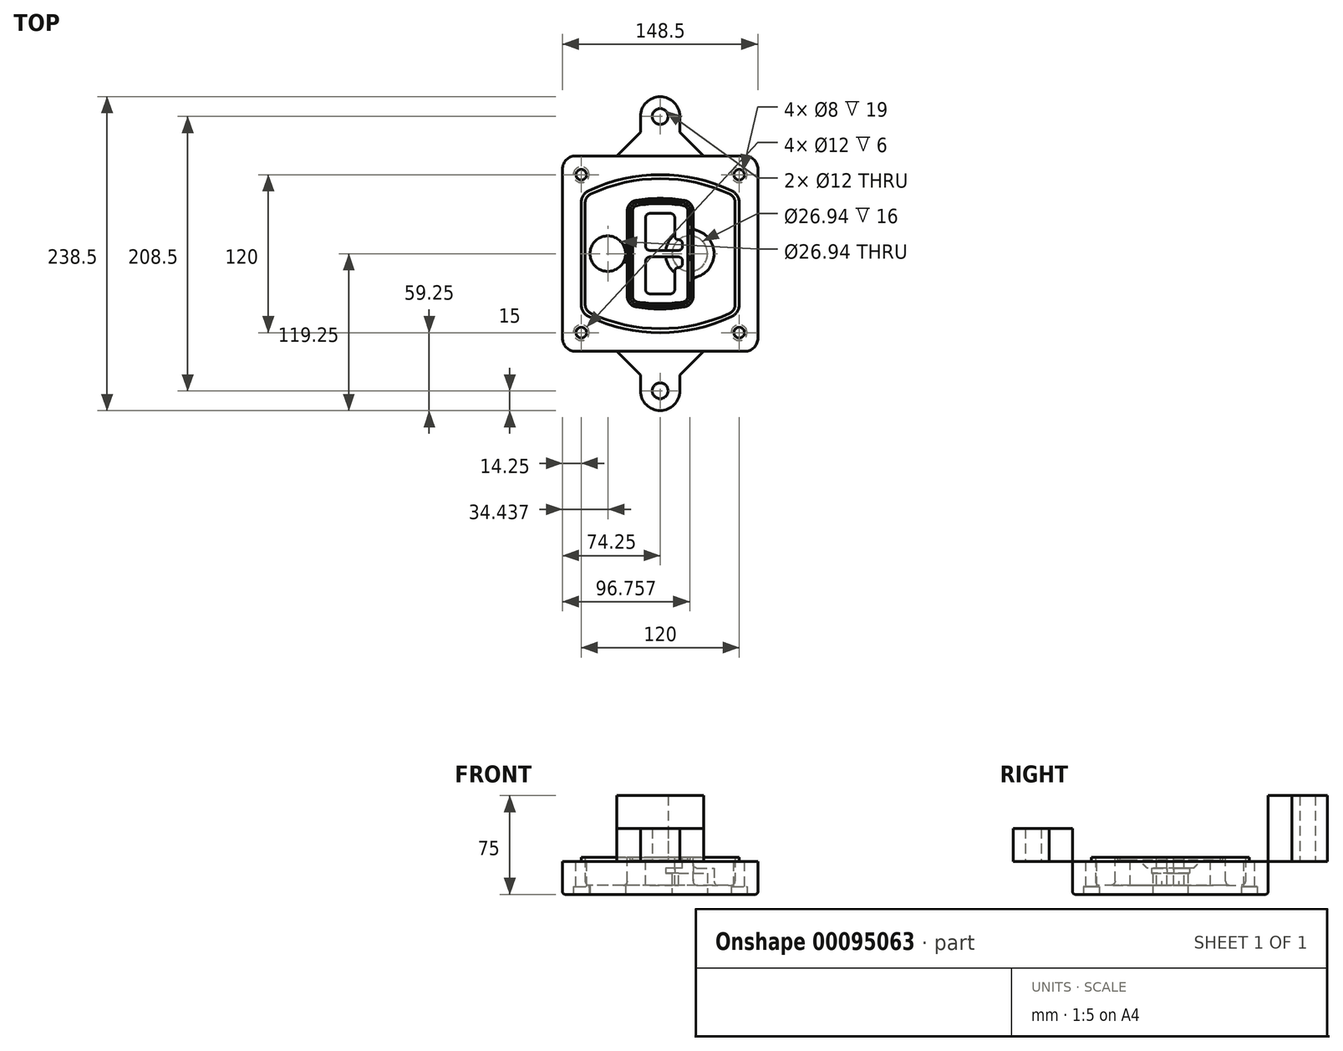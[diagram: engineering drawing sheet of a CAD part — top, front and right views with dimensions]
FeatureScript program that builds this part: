
annotation { "Feature Type Name" : "Feature", "Feature Type Description" : "" }
export const myFeature = defineFeature(function(context is Context, id is Id, definition is map)
    precondition{}
    {
        {
            var Q0;
            Q0=qCreatedBy(makeId("Top.planeOp"),FACE);
            var sketch = newSketch(context, id + "F0", { "sketchPlane" : qUnion([Q0])});
            skPoint(sketch, "E0.rect.middle", {"position": v(0, 0) * mm});
            skLineSegment(sketch, "E1.bottom", {"start": v(-64.25, -74.25) * mm, "end": v(64.25, -74.25) * mm});
            skLineSegment(sketch, "E1.top", {"start": v(-64.25, 74.25) * mm, "end": v(64.25, 74.25) * mm});
            skLineSegment(sketch, "E1.left", {"start": v(-74.25, -64.25) * mm, "end": v(-74.25, 64.25) * mm});
            skLineSegment(sketch, "E1.right", {"start": v(74.25, -64.25) * mm, "end": v(74.25, 64.25) * mm});
            skLineSegment(sketch, "E2", {"start": v(-74.25, 74.25) * mm, "end": v(74.25, -74.25) * mm, "construction": true});
            skLineSegment(sketch, "E3", {"start": v(74.25, 74.25) * mm, "end": v(-74.25, -74.25) * mm, "construction": true});
            skCircle(sketch, "E4", {"center": v(-60, 60) * mm, "radius": 4 * mm});
            skCircle(sketch, "E5", {"center": v(60, 60) * mm, "radius": 4 * mm});
            skCircle(sketch, "E6", {"center": v(60, -60) * mm, "radius": 4 * mm});
            skCircle(sketch, "E7", {"center": v(-60, -60) * mm, "radius": 4 * mm});
            skLineSegment(sketch, "E8", {"start": v(-60, 60) * mm, "end": v(60, 60) * mm, "construction": true});
            skLineSegment(sketch, "E9", {"start": v(60, 60) * mm, "end": v(60, -60) * mm, "construction": true});
            skLineSegment(sketch, "E10", {"start": v(60, -60) * mm, "end": v(-60, -60) * mm, "construction": true});
            skLineSegment(sketch, "E11", {"start": v(-60, -60) * mm, "end": v(-60, 60) * mm, "construction": true});
            skLineSegment(sketch, "E12", {"start": v(-60, 38.83) * mm, "end": v(-60, -38.83) * mm});
            skLineSegment(sketch, "E13", {"start": v(60, 38.83) * mm, "end": v(60, -38.83) * mm});
            skArc(sketch, "E14", {"start": v(54.26, 47.88) * mm, "mid": v(0, 60) * mm, "end": v(-54.26, 47.88) * mm});
            skArc(sketch, "E15", {"start": v(-54.26, -47.88) * mm, "mid": v(0, -60) * mm, "end": v(54.26, -47.88) * mm});
            skLineSegment(sketch, "E16", {"start": v(-60, 0) * mm, "end": v(60, 0) * mm, "construction": true});
            skPoint(sketch, "E17.visualSharp", {"position": v(-60, -45) * mm});
            skArc(sketch, "E17.filletArc", {"start": v(-60, -38.83) * mm, "mid": v(-58.44, -44.2) * mm, "end": v(-54.26, -47.88) * mm});
            skPoint(sketch, "E18.visualSharp", {"position": v(-60, 45) * mm});
            skArc(sketch, "E18.filletArc", {"start": v(-54.26, 47.88) * mm, "mid": v(-58.44, 44.2) * mm, "end": v(-60, 38.83) * mm});
            skPoint(sketch, "E19.visualSharp", {"position": v(60, 45) * mm});
            skArc(sketch, "E19.filletArc", {"start": v(60, 38.83) * mm, "mid": v(58.44, 44.2) * mm, "end": v(54.26, 47.88) * mm});
            skPoint(sketch, "E20.visualSharp", {"position": v(60, -45) * mm});
            skArc(sketch, "E20.filletArc", {"start": v(54.26, -47.88) * mm, "mid": v(58.44, -44.2) * mm, "end": v(60, -38.83) * mm});
            skPoint(sketch, "E21.visualSharp", {"position": v(-74.25, 74.25) * mm});
            skArc(sketch, "E21.filletArc", {"start": v(-64.25, 74.25) * mm, "mid": v(-71.32, 71.32) * mm, "end": v(-74.25, 64.25) * mm});
            skPoint(sketch, "E22.visualSharp", {"position": v(74.25, 74.25) * mm});
            skArc(sketch, "E22.filletArc", {"start": v(74.25, 64.25) * mm, "mid": v(71.32, 71.32) * mm, "end": v(64.25, 74.25) * mm});
            skPoint(sketch, "E23.visualSharp", {"position": v(74.25, -74.25) * mm});
            skArc(sketch, "E23.filletArc", {"start": v(64.25, -74.25) * mm, "mid": v(71.32, -71.32) * mm, "end": v(74.25, -64.25) * mm});
            skPoint(sketch, "E24.visualSharp", {"position": v(-74.25, -74.25) * mm});
            skArc(sketch, "E24.filletArc", {"start": v(-74.25, -64.25) * mm, "mid": v(-71.32, -71.32) * mm, "end": v(-64.25, -74.25) * mm});
            skArc(sketch, "E25.0", {"start": v(57, 38.83) * mm, "mid": v(55.9, 42.58) * mm, "end": v(52.98, 45.17) * mm});
            skLineSegment(sketch, "E25.1", {"start": v(57, 38.83) * mm, "end": v(57, -38.83) * mm});
            skArc(sketch, "E25.2", {"start": v(52.98, -45.17) * mm, "mid": v(55.9, -42.58) * mm, "end": v(57, -38.83) * mm});
            skArc(sketch, "E25.3", {"start": v(-52.98, -45.17) * mm, "mid": v(0, -57) * mm, "end": v(52.98, -45.17) * mm});
            skArc(sketch, "E25.4", {"start": v(-57, -38.83) * mm, "mid": v(-55.9, -42.58) * mm, "end": v(-52.98, -45.17) * mm});
            skArc(sketch, "E25.5", {"start": v(52.98, 45.17) * mm, "mid": v(0, 57) * mm, "end": v(-52.98, 45.17) * mm});
            skLineSegment(sketch, "E25.6", {"start": v(-57, 38.83) * mm, "end": v(-57, -38.83) * mm});
            skArc(sketch, "E25.7", {"start": v(-52.98, 45.17) * mm, "mid": v(-55.9, 42.58) * mm, "end": v(-57, 38.83) * mm});
            skArc(sketch, "E26.0", {"start": v(-55.96, 51.5) * mm, "mid": v(-61.82, 46.33) * mm, "end": v(-64, 38.83) * mm});
            skArc(sketch, "E26.1", {"start": v(55.96, 51.5) * mm, "mid": v(0, 64) * mm, "end": v(-55.96, 51.5) * mm});
            skArc(sketch, "E26.2", {"start": v(64, 38.83) * mm, "mid": v(61.82, 46.33) * mm, "end": v(55.96, 51.5) * mm});
            skLineSegment(sketch, "E26.3", {"start": v(64, 38.83) * mm, "end": v(64, -38.83) * mm});
            skArc(sketch, "E26.4", {"start": v(55.96, -51.5) * mm, "mid": v(61.82, -46.33) * mm, "end": v(64, -38.83) * mm});
            skLineSegment(sketch, "E26.5", {"start": v(-64, 38.83) * mm, "end": v(-64, -38.83) * mm});
            skArc(sketch, "E26.6", {"start": v(-55.96, -51.5) * mm, "mid": v(0, -64) * mm, "end": v(55.96, -51.5) * mm});
            skArc(sketch, "E26.7", {"start": v(-64, -38.83) * mm, "mid": v(-61.82, -46.33) * mm, "end": v(-55.96, -51.5) * mm});
            skSolve(sketch);
        }
        {
            var Q0;
            Q0=makeQuery(id+"F0.imprint","IMPRINT",FACE,{"disambiguationData":[TD([[makeQuery(id+"F0.imprint","IMPRINT",EDGE,{"derivedFrom":sQuery(id+"F0.wireOp",EDGE,"E1.bottom")}),1.0]])]});
            var Q1;
            Q1=makeQuery(id+"F0.imprint","IMPRINT",FACE,{"disambiguationData":[TD([[makeQuery(id+"F0.imprint","IMPRINT",EDGE,{"derivedFrom":sQuery(id+"F0.wireOp",EDGE,"E12")}),1.0]])]});
            var Q2;
            Q2=makeQuery(id+"F0.imprint","IMPRINT",FACE,{"disambiguationData":[TD([[makeQuery(id+"F0.imprint","IMPRINT",EDGE,{"derivedFrom":sQuery(id+"F0.wireOp",EDGE,"E25.0")}),1.0]])]});
            var Q3;
            Q3=makeQuery(id+"F0.imprint","IMPRINT",FACE,{"disambiguationData":[TD([[makeQuery(id+"F0.imprint","IMPRINT",EDGE,{"derivedFrom":sQuery(id+"F0.wireOp",EDGE,"E12")}),-1.0]])]});
            extrude(context, id + "F1", {"entities" : qUnion([Q0, Q1, Q2, Q3]), "oppositeDirection" : true, "depth" : 25 * mm});
        }
        {
            var Q0;
            Q0=makeQuery(id+"F0.imprint","IMPRINT",FACE,{"disambiguationData":[TD([[makeQuery(id+"F0.imprint","IMPRINT",EDGE,{"derivedFrom":sQuery(id+"F0.wireOp",EDGE,"E12")}),1.0]])]});
            extrude(context, id + "F2", {"entities" : qUnion([Q0]), "operationType" : NewBodyOperationType.ADD, "depth" : 3 * mm});
        }
        {
            var Q0;
            Q0=makeQuery(id+"F0.imprint","IMPRINT",FACE,{"disambiguationData":[TD([[makeQuery(id+"F0.imprint","IMPRINT",EDGE,{"derivedFrom":sQuery(id+"F0.wireOp",EDGE,"E25.0")}),1.0]])]});
            extrude(context, id + "F3", {"entities" : qUnion([Q0]), "operationType" : NewBodyOperationType.REMOVE, "oppositeDirection" : true, "depth" : 18 * mm});
        }
        {
            var Q0;
            Q0=makeQuery(id+"F2.opExtrude","CAP_FACE",FACE,{"disambiguationData":[OSD([sQuery(id+"F0.wireOp",EDGE,"E12"),sQuery(id+"F0.wireOp",EDGE,"E13"),sQuery(id+"F0.wireOp",EDGE,"E14"),sQuery(id+"F0.wireOp",EDGE,"E15"),sQuery(id+"F0.wireOp",EDGE,"E17.filletArc"),sQuery(id+"F0.wireOp",EDGE,"E18.filletArc"),sQuery(id+"F0.wireOp",EDGE,"E19.filletArc"),sQuery(id+"F0.wireOp",EDGE,"E20.filletArc"),sQuery(id+"F0.wireOp",EDGE,"E25.0"),sQuery(id+"F0.wireOp",EDGE,"E25.1"),sQuery(id+"F0.wireOp",EDGE,"E25.2"),sQuery(id+"F0.wireOp",EDGE,"E25.3"),sQuery(id+"F0.wireOp",EDGE,"E25.4"),sQuery(id+"F0.wireOp",EDGE,"E25.5"),sQuery(id+"F0.wireOp",EDGE,"E25.6"),sQuery(id+"F0.wireOp",EDGE,"E25.7")])],"isStart":false});
            var sketch = newSketch(context, id + "F4", { "sketchPlane" : qUnion([Q0])});
            skArc(sketch, "E27.0", {"start": v(-18.34, -40.45) * mm, "mid": v(0, -42) * mm, "end": v(18.34, -40.45) * mm});
            skArc(sketch, "E28.0", {"start": v(18.34, 40.45) * mm, "mid": v(0, 42) * mm, "end": v(-18.34, 40.45) * mm});
            skLineSegment(sketch, "E29", {"start": v(-25, 32.57) * mm, "end": v(-25, -32.57) * mm});
            skLineSegment(sketch, "E30", {"start": v(25, 32.57) * mm, "end": v(25, -32.57) * mm});
            skLineSegment(sketch, "E31", {"start": v(-25, 39.1) * mm, "end": v(25, 39.1) * mm, "construction": true});
            skLineSegment(sketch, "E32", {"start": v(-25, -39.1) * mm, "end": v(25, -39.1) * mm, "construction": true});
            skPoint(sketch, "E33.visualSharp", {"position": v(-25, 39.1) * mm});
            skArc(sketch, "E33.filletArc", {"start": v(-18.34, 40.45) * mm, "mid": v(-23.11, 37.73) * mm, "end": v(-25, 32.57) * mm});
            skPoint(sketch, "E34.visualSharp", {"position": v(25, 39.1) * mm});
            skArc(sketch, "E34.filletArc", {"start": v(25, 32.57) * mm, "mid": v(23.11, 37.73) * mm, "end": v(18.34, 40.45) * mm});
            skPoint(sketch, "E35.visualSharp", {"position": v(25, -39.1) * mm});
            skArc(sketch, "E35.filletArc", {"start": v(18.34, -40.45) * mm, "mid": v(23.11, -37.73) * mm, "end": v(25, -32.57) * mm});
            skPoint(sketch, "E36.visualSharp", {"position": v(-25, -39.1) * mm});
            skArc(sketch, "E36.filletArc", {"start": v(-25, -32.57) * mm, "mid": v(-23.11, -37.73) * mm, "end": v(-18.34, -40.45) * mm});
            skArc(sketch, "E37.0", {"start": v(52.98, 45.17) * mm, "mid": v(0, 57) * mm, "end": v(-52.98, 45.17) * mm});
            skArc(sketch, "E37.1", {"start": v(-52.98, 45.17) * mm, "mid": v(-55.9, 42.58) * mm, "end": v(-57, 38.83) * mm});
            skLineSegment(sketch, "E37.2", {"start": v(-57, 38.83) * mm, "end": v(-57, -38.83) * mm});
            skArc(sketch, "E37.3", {"start": v(-57, -38.83) * mm, "mid": v(-55.9, -42.58) * mm, "end": v(-52.98, -45.17) * mm});
            skArc(sketch, "E37.4", {"start": v(-52.98, -45.17) * mm, "mid": v(0, -57) * mm, "end": v(52.98, -45.17) * mm});
            skArc(sketch, "E37.5", {"start": v(52.98, -45.17) * mm, "mid": v(55.9, -42.58) * mm, "end": v(57, -38.83) * mm});
            skLineSegment(sketch, "E37.6", {"start": v(57, 38.83) * mm, "end": v(57, -38.83) * mm});
            skArc(sketch, "E37.7", {"start": v(57, 38.83) * mm, "mid": v(55.9, 42.58) * mm, "end": v(52.98, 45.17) * mm});
            skLineSegment(sketch, "E38.0", {"start": v(23, 32.57) * mm, "end": v(23, -32.57) * mm});
            skArc(sketch, "E38.1", {"start": v(18, -38.48) * mm, "mid": v(21.58, -36.44) * mm, "end": v(23, -32.57) * mm});
            skArc(sketch, "E38.2", {"start": v(-18, -38.48) * mm, "mid": v(0, -40) * mm, "end": v(18, -38.48) * mm});
            skArc(sketch, "E38.3", {"start": v(-23, -32.57) * mm, "mid": v(-21.58, -36.44) * mm, "end": v(-18, -38.48) * mm});
            skLineSegment(sketch, "E38.4", {"start": v(-23, 32.57) * mm, "end": v(-23, -32.57) * mm});
            skArc(sketch, "E38.5", {"start": v(23, 32.57) * mm, "mid": v(21.58, 36.44) * mm, "end": v(18, 38.48) * mm});
            skArc(sketch, "E38.6", {"start": v(-18, 38.48) * mm, "mid": v(-21.58, 36.44) * mm, "end": v(-23, 32.57) * mm});
            skArc(sketch, "E38.7", {"start": v(18, 38.48) * mm, "mid": v(0, 40) * mm, "end": v(-18, 38.48) * mm});
            skArc(sketch, "E39.0", {"start": v(21, 32.57) * mm, "mid": v(20.06, 35.15) * mm, "end": v(17.67, 36.5) * mm});
            skLineSegment(sketch, "E39.1", {"start": v(21, 32.57) * mm, "end": v(21, -32.57) * mm});
            skArc(sketch, "E39.2", {"start": v(17.67, -36.5) * mm, "mid": v(20.06, -35.15) * mm, "end": v(21, -32.57) * mm});
            skArc(sketch, "E39.3", {"start": v(-17.67, -36.5) * mm, "mid": v(0, -38) * mm, "end": v(17.67, -36.5) * mm});
            skArc(sketch, "E39.4", {"start": v(-21, -32.57) * mm, "mid": v(-20.06, -35.15) * mm, "end": v(-17.67, -36.5) * mm});
            skArc(sketch, "E39.5", {"start": v(17.67, 36.5) * mm, "mid": v(0, 38) * mm, "end": v(-17.67, 36.5) * mm});
            skLineSegment(sketch, "E39.6", {"start": v(-21, 32.57) * mm, "end": v(-21, -32.57) * mm});
            skArc(sketch, "E39.7", {"start": v(-17.67, 36.5) * mm, "mid": v(-20.06, 35.15) * mm, "end": v(-21, 32.57) * mm});
            skLineSegment(sketch, "E40", {"start": v(-25, 0) * mm, "end": v(25, 0) * mm, "construction": true});
            skLineSegment(sketch, "E41", {"start": v(-11, 5.5) * mm, "end": v(-11, 27.5) * mm});
            skLineSegment(sketch, "E42", {"start": v(-8, 30.5) * mm, "end": v(8, 30.5) * mm});
            skLineSegment(sketch, "E43", {"start": v(11, 27.5) * mm, "end": v(11, 13.5) * mm});
            skLineSegment(sketch, "E44", {"start": v(14, 10.5) * mm, "end": v(14, 10.5) * mm});
            skLineSegment(sketch, "E45", {"start": v(17, 7.5) * mm, "end": v(17, 5.5) * mm});
            skLineSegment(sketch, "E46", {"start": v(14, 2.5) * mm, "end": v(-8, 2.5) * mm});
            skPoint(sketch, "E47.visualSharp", {"position": v(-11, 30.5) * mm});
            skArc(sketch, "E47.filletArc", {"start": v(-8, 30.5) * mm, "mid": v(-10.12, 29.62) * mm, "end": v(-11, 27.5) * mm});
            skPoint(sketch, "E48.visualSharp", {"position": v(11, 30.5) * mm});
            skArc(sketch, "E48.filletArc", {"start": v(11, 27.5) * mm, "mid": v(10.12, 29.62) * mm, "end": v(8, 30.5) * mm});
            skPoint(sketch, "E49.visualSharp", {"position": v(11, 10.5) * mm});
            skArc(sketch, "E49.filletArc", {"start": v(11, 13.5) * mm, "mid": v(11.88, 11.38) * mm, "end": v(14, 10.5) * mm});
            skPoint(sketch, "E50.visualSharp", {"position": v(17, 10.5) * mm});
            skArc(sketch, "E50.filletArc", {"start": v(17, 7.5) * mm, "mid": v(16.12, 9.62) * mm, "end": v(14, 10.5) * mm});
            skPoint(sketch, "E51.visualSharp", {"position": v(17, 2.5) * mm});
            skArc(sketch, "E51.filletArc", {"start": v(14, 2.5) * mm, "mid": v(16.12, 3.38) * mm, "end": v(17, 5.5) * mm});
            skPoint(sketch, "E52.visualSharp", {"position": v(-11, 2.5) * mm});
            skArc(sketch, "E52.filletArc", {"start": v(-11, 5.5) * mm, "mid": v(-10.12, 3.38) * mm, "end": v(-8, 2.5) * mm});
            skLineSegment(sketch, "E53.0.MirrorCS", {"start": v(14, -2.5) * mm, "end": v(-8, -2.5) * mm});
            skArc(sketch, "E54.0.MirrorCS", {"start": v(-11, -5.5) * mm, "mid": v(-10.12, -3.38) * mm, "end": v(-8, -2.5) * mm});
            skLineSegment(sketch, "E55.0.MirrorCS", {"start": v(-11, -5.5) * mm, "end": v(-11, -27.5) * mm});
            skArc(sketch, "E56.0.MirrorCS", {"start": v(-8, -30.5) * mm, "mid": v(-10.12, -29.62) * mm, "end": v(-11, -27.5) * mm});
            skLineSegment(sketch, "E57.0.MirrorCS", {"start": v(-8, -30.5) * mm, "end": v(8, -30.5) * mm});
            skArc(sketch, "E58.0.MirrorCS", {"start": v(11, -27.5) * mm, "mid": v(10.12, -29.62) * mm, "end": v(8, -30.5) * mm});
            skLineSegment(sketch, "E59.0.MirrorCS", {"start": v(11, -27.5) * mm, "end": v(11, -13.5) * mm});
            skArc(sketch, "E60.0.MirrorCS", {"start": v(11, -13.5) * mm, "mid": v(11.88, -11.38) * mm, "end": v(14, -10.5) * mm});
            skArc(sketch, "E61.0.MirrorCS", {"start": v(17, -7.5) * mm, "mid": v(16.12, -9.62) * mm, "end": v(14, -10.5) * mm});
            skLineSegment(sketch, "E62.0.MirrorCS", {"start": v(17, -7.5) * mm, "end": v(17, -5.5) * mm});
            skArc(sketch, "E63.0.MirrorCS", {"start": v(14, -2.5) * mm, "mid": v(16.12, -3.38) * mm, "end": v(17, -5.5) * mm});
            skSolve(sketch);
        }
        {
            var Q0;
            Q0=makeQuery(id+"F4.imprint","IMPRINT",FACE,{"disambiguationData":[TD([[makeQuery(id+"F4.imprint","IMPRINT",EDGE,{"derivedFrom":sQuery(id+"F4.wireOp",EDGE,"E27.0")}),1.0]])]});
            var Q1;
            Q1=makeQuery(id+"F4.imprint","IMPRINT",FACE,{"disambiguationData":[TD([[makeQuery(id+"F4.imprint","IMPRINT",EDGE,{"derivedFrom":sQuery(id+"F4.wireOp",EDGE,"E38.0")}),-1.0]])]});
            var Q2;
            Q2=makeQuery(id+"F4.imprint","IMPRINT",FACE,{"disambiguationData":[TD([[makeQuery(id+"F4.imprint","IMPRINT",EDGE,{"derivedFrom":sQuery(id+"F4.wireOp",EDGE,"E39.0")}),1.0]])]});
            extrude(context, id + "F5", {"entities" : qUnion([Q0, Q1, Q2]), "operationType" : NewBodyOperationType.ADD, "endBound" : BoundingType.UP_TO_NEXT, "oppositeDirection" : true, "depth" : 25 * mm});
        }
        {
            var Q0;
            Q0=makeQuery(id+"F4.imprint","IMPRINT",FACE,{"disambiguationData":[TD([[makeQuery(id+"F4.imprint","IMPRINT",EDGE,{"derivedFrom":sQuery(id+"F4.wireOp",EDGE,"E38.0")}),-1.0]])]});
            extrude(context, id + "F6", {"entities" : qUnion([Q0]), "operationType" : NewBodyOperationType.REMOVE, "oppositeDirection" : true, "depth" : 2 * mm});
        }
        {
            var Q0;
            Q0=makeQuery(id+"F1.opExtrude","CAP_FACE",FACE,{"disambiguationData":[OSD([sQuery(id+"F0.wireOp",EDGE,"E1.bottom"),sQuery(id+"F0.wireOp",EDGE,"E1.top"),sQuery(id+"F0.wireOp",EDGE,"E1.left"),sQuery(id+"F0.wireOp",EDGE,"E1.right"),sQuery(id+"F0.wireOp",EDGE,"E4"),sQuery(id+"F0.wireOp",EDGE,"E5"),sQuery(id+"F0.wireOp",EDGE,"E6"),sQuery(id+"F0.wireOp",EDGE,"E7"),sQuery(id+"F0.wireOp",EDGE,"E21.filletArc"),sQuery(id+"F0.wireOp",EDGE,"E22.filletArc"),sQuery(id+"F0.wireOp",EDGE,"E23.filletArc"),sQuery(id+"F0.wireOp",EDGE,"E24.filletArc")])],"isStart":false});
            var sketch = newSketch(context, id + "F7", { "sketchPlane" : qUnion([Q0])});
            skCircle(sketch, "E64", {"center": v(22.5, 0) * mm, "radius": 13.47 * mm});
            skCircle(sketch, "E65", {"center": v(-39.81, 0) * mm, "radius": 13.47 * mm});
            skLineSegment(sketch, "E66", {"start": v(74.25, 0) * mm, "end": v(-74.25, 0) * mm});
            skCircle(sketch, "E67", {"center": v(22.5, 0) * mm, "radius": 18.47 * mm});
            skCircle(sketch, "E68", {"center": v(60, -60) * mm, "radius": 6 * mm});
            skCircle(sketch, "E69", {"center": v(-60, -60) * mm, "radius": 6 * mm});
            skCircle(sketch, "E70", {"center": v(-60, 60) * mm, "radius": 6 * mm});
            skCircle(sketch, "E71", {"center": v(60, 60) * mm, "radius": 6 * mm});
            skSolve(sketch);
        }
        {
            var Q0;
            {var subQ1=sQuery(id+"F7.wireOp",EDGE,"E66");var subQ4=sQuery(id+"F7.wireOp",EDGE,"E64");var subQ6=makeQuery(id+"F7.imprint","INTERSECT",VERTEX,{"disambiguationData":[OD(0.0)],"derivedFrom":[subQ4,subQ1]});Q0=makeQuery(id+"F7.imprint","IMPRINT",FACE,{"disambiguationData":[TD([[makeQuery(id+"F7.imprint","IMPRINT",EDGE,{"disambiguationData":[TD([[subQ6,-1.0]])],"derivedFrom":subQ4}),-1.0]])]});}
            var Q1;
            {var subQ0=sQuery(id+"F7.wireOp",EDGE,"E66");var subQ1=sQuery(id+"F7.wireOp",EDGE,"E64");var subQ3=makeQuery(id+"F7.imprint","INTERSECT",VERTEX,{"disambiguationData":[OD(0.0)],"derivedFrom":[subQ1,subQ0]});Q1=makeQuery(id+"F7.imprint","IMPRINT",FACE,{"disambiguationData":[TD([[makeQuery(id+"F7.imprint","IMPRINT",EDGE,{"disambiguationData":[TD([[subQ3,-1.0]])],"derivedFrom":subQ1}),1.0]])]});}
            var Q2;
            {var subQ0=sQuery(id+"F7.wireOp",EDGE,"E66");var subQ1=sQuery(id+"F7.wireOp",EDGE,"E64");var subQ3=makeQuery(id+"F7.imprint","INTERSECT",VERTEX,{"disambiguationData":[OD(0.0)],"derivedFrom":[subQ1,subQ0]});Q2=makeQuery(id+"F7.imprint","IMPRINT",FACE,{"disambiguationData":[TD([[makeQuery(id+"F7.imprint","IMPRINT",EDGE,{"disambiguationData":[TD([[subQ3,1.0]])],"derivedFrom":subQ1}),1.0]])]});}
            var Q3;
            {var subQ1=sQuery(id+"F7.wireOp",EDGE,"E66");var subQ4=sQuery(id+"F7.wireOp",EDGE,"E64");var subQ6=makeQuery(id+"F7.imprint","INTERSECT",VERTEX,{"disambiguationData":[OD(0.0)],"derivedFrom":[subQ4,subQ1]});Q3=makeQuery(id+"F7.imprint","IMPRINT",FACE,{"disambiguationData":[TD([[makeQuery(id+"F7.imprint","IMPRINT",EDGE,{"disambiguationData":[TD([[subQ6,1.0]])],"derivedFrom":subQ4}),-1.0]])]});}
            extrude(context, id + "F8", {"entities" : qUnion([Q0, Q1, Q2, Q3]), "operationType" : NewBodyOperationType.ADD, "oppositeDirection" : true, "depth" : 20 * mm});
        }
        {
            var Q0;
            {var subQ0=sQuery(id+"F7.wireOp",EDGE,"E66");var subQ1=sQuery(id+"F7.wireOp",EDGE,"E64");var subQ3=makeQuery(id+"F7.imprint","INTERSECT",VERTEX,{"disambiguationData":[OD(0.0)],"derivedFrom":[subQ1,subQ0]});Q0=makeQuery(id+"F7.imprint","IMPRINT",FACE,{"disambiguationData":[TD([[makeQuery(id+"F7.imprint","IMPRINT",EDGE,{"disambiguationData":[TD([[subQ3,-1.0]])],"derivedFrom":subQ1}),1.0]])]});}
            var Q1;
            {var subQ0=sQuery(id+"F7.wireOp",EDGE,"E66");var subQ1=sQuery(id+"F7.wireOp",EDGE,"E64");var subQ3=makeQuery(id+"F7.imprint","INTERSECT",VERTEX,{"disambiguationData":[OD(0.0)],"derivedFrom":[subQ1,subQ0]});Q1=makeQuery(id+"F7.imprint","IMPRINT",FACE,{"disambiguationData":[TD([[makeQuery(id+"F7.imprint","IMPRINT",EDGE,{"disambiguationData":[TD([[subQ3,1.0]])],"derivedFrom":subQ1}),1.0]])]});}
            extrude(context, id + "F9", {"entities" : qUnion([Q0, Q1]), "operationType" : NewBodyOperationType.REMOVE, "oppositeDirection" : true, "depth" : 16 * mm});
        }
        {
            var Q0;
            {var subQ0=sQuery(id+"F7.wireOp",EDGE,"E66");var subQ1=sQuery(id+"F7.wireOp",EDGE,"E65");var subQ3=makeQuery(id+"F7.imprint","INTERSECT",VERTEX,{"disambiguationData":[OD(0.0)],"derivedFrom":[subQ1,subQ0]});Q0=makeQuery(id+"F7.imprint","IMPRINT",FACE,{"disambiguationData":[TD([[makeQuery(id+"F7.imprint","IMPRINT",EDGE,{"disambiguationData":[TD([[subQ3,-1.0]])],"derivedFrom":subQ1}),1.0]])]});}
            var Q1;
            {var subQ0=sQuery(id+"F7.wireOp",EDGE,"E66");var subQ1=sQuery(id+"F7.wireOp",EDGE,"E65");var subQ3=makeQuery(id+"F7.imprint","INTERSECT",VERTEX,{"disambiguationData":[OD(0.0)],"derivedFrom":[subQ1,subQ0]});Q1=makeQuery(id+"F7.imprint","IMPRINT",FACE,{"disambiguationData":[TD([[makeQuery(id+"F7.imprint","IMPRINT",EDGE,{"disambiguationData":[TD([[subQ3,1.0]])],"derivedFrom":subQ1}),1.0]])]});}
            extrude(context, id + "F10", {"entities" : qUnion([Q0, Q1]), "operationType" : NewBodyOperationType.REMOVE, "oppositeDirection" : true, "depth" : 25 * mm});
        }
        {
            var Q0;
            Q0=makeQuery(id+"F7.imprint","IMPRINT",FACE,{"disambiguationData":[TD([[makeQuery(id+"F7.imprint","IMPRINT",EDGE,{"derivedFrom":sQuery(id+"F7.wireOp",EDGE,"E68")}),1.0]])]});
            var Q1;
            Q1=makeQuery(id+"F7.imprint","IMPRINT",FACE,{"disambiguationData":[TD([[makeQuery(id+"F7.imprint","IMPRINT",EDGE,{"derivedFrom":makeQuery(id+"F1.opExtrude","CAP_EDGE",EDGE,{"disambiguationData":[OSD([sQuery(id+"F0.wireOp",EDGE,"E5")])],"isStart":false})}),-1.0]])]});
            var Q2;
            Q2=makeQuery(id+"F7.imprint","IMPRINT",FACE,{"disambiguationData":[TD([[makeQuery(id+"F7.imprint","IMPRINT",EDGE,{"derivedFrom":sQuery(id+"F7.wireOp",EDGE,"E69")}),1.0]])]});
            var Q3;
            Q3=makeQuery(id+"F7.imprint","IMPRINT",FACE,{"disambiguationData":[TD([[makeQuery(id+"F7.imprint","IMPRINT",EDGE,{"derivedFrom":makeQuery(id+"F1.opExtrude","CAP_EDGE",EDGE,{"disambiguationData":[OSD([sQuery(id+"F0.wireOp",EDGE,"E4")])],"isStart":false})}),-1.0]])]});
            var Q4;
            Q4=makeQuery(id+"F7.imprint","IMPRINT",FACE,{"disambiguationData":[TD([[makeQuery(id+"F7.imprint","IMPRINT",EDGE,{"derivedFrom":sQuery(id+"F7.wireOp",EDGE,"E70")}),1.0]])]});
            var Q5;
            Q5=makeQuery(id+"F7.imprint","IMPRINT",FACE,{"disambiguationData":[TD([[makeQuery(id+"F7.imprint","IMPRINT",EDGE,{"derivedFrom":makeQuery(id+"F1.opExtrude","CAP_EDGE",EDGE,{"disambiguationData":[OSD([sQuery(id+"F0.wireOp",EDGE,"E7")])],"isStart":false})}),-1.0]])]});
            var Q6;
            Q6=makeQuery(id+"F7.imprint","IMPRINT",FACE,{"disambiguationData":[TD([[makeQuery(id+"F7.imprint","IMPRINT",EDGE,{"derivedFrom":sQuery(id+"F7.wireOp",EDGE,"E71")}),1.0]])]});
            var Q7;
            Q7=makeQuery(id+"F7.imprint","IMPRINT",FACE,{"disambiguationData":[TD([[makeQuery(id+"F7.imprint","IMPRINT",EDGE,{"derivedFrom":makeQuery(id+"F1.opExtrude","CAP_EDGE",EDGE,{"disambiguationData":[OSD([sQuery(id+"F0.wireOp",EDGE,"E6")])],"isStart":false})}),-1.0]])]});
            extrude(context, id + "F11", {"entities" : qUnion([Q0, Q1, Q2, Q3, Q4, Q5, Q6, Q7]), "operationType" : NewBodyOperationType.REMOVE, "oppositeDirection" : true, "depth" : 6 * mm});
        }
        {
            var Q0;
            Q0=makeQuery(id+"F9.boolean.opBoolean","COPY",FACE,{"derivedFrom":makeQuery(id+"F9.opExtrude","CAP_FACE",FACE,{"disambiguationData":[OSD([sQuery(id+"F7.wireOp",EDGE,"E64")])],"isStart":false})});
            var sketch = newSketch(context, id + "F12", { "sketchPlane" : qUnion([Q0])});
            skArc(sketch, "E72.0", {"start": v(11, 14.45) * mm, "mid": v(6.45, 9.13) * mm, "end": v(4.2, 2.5) * mm});
            skArc(sketch, "E72.1", {"start": v(4.2, -2.5) * mm, "mid": v(6.45, -9.13) * mm, "end": v(11, -14.45) * mm});
            skLineSegment(sketch, "E73", {"start": v(4.2, -2.5) * mm, "end": v(14, -2.5) * mm});
            skLineSegment(sketch, "E74.0", {"start": v(14, 2.5) * mm, "end": v(4.2, 2.5) * mm});
            skArc(sketch, "E74.1", {"start": v(14, 2.5) * mm, "mid": v(16.12, 3.38) * mm, "end": v(17, 5.5) * mm});
            skLineSegment(sketch, "E74.2", {"start": v(17, 7.5) * mm, "end": v(17, 5.5) * mm});
            skArc(sketch, "E74.3", {"start": v(17, 7.5) * mm, "mid": v(16.12, 9.62) * mm, "end": v(14, 10.5) * mm});
            skArc(sketch, "E74.4", {"start": v(11, 13.5) * mm, "mid": v(11.88, 11.38) * mm, "end": v(14, 10.5) * mm});
            skLineSegment(sketch, "E74.5", {"start": v(11, 14.45) * mm, "end": v(11, 13.5) * mm});
            skLineSegment(sketch, "E74.7", {"start": v(14, -2.5) * mm, "end": v(4.2, -2.5) * mm});
            skArc(sketch, "E74.8", {"start": v(14, -2.5) * mm, "mid": v(16.12, -3.38) * mm, "end": v(17, -5.5) * mm});
            skLineSegment(sketch, "E74.9", {"start": v(17, -7.5) * mm, "end": v(17, -5.5) * mm});
            skArc(sketch, "E74.10", {"start": v(17, -7.5) * mm, "mid": v(16.12, -9.62) * mm, "end": v(14, -10.5) * mm});
            skArc(sketch, "E74.11", {"start": v(11, -13.5) * mm, "mid": v(11.88, -11.38) * mm, "end": v(14, -10.5) * mm});
            skLineSegment(sketch, "E74.12", {"start": v(11, -14.45) * mm, "end": v(11, -13.5) * mm});
            skPoint(sketch, "E75.orphan", {"position": v(11, -27.5) * mm});
            skPoint(sketch, "E76.orphan", {"position": v(-8, -2.5) * mm});
            skPoint(sketch, "E77.orphan", {"position": v(-8, 2.5) * mm});
            skPoint(sketch, "E78.orphan", {"position": v(11, 27.5) * mm});
            skSolve(sketch);
        }
        {
            var Q0;
            {var subQ7=sQuery(id+"F12.wireOp",EDGE,"E72.0");var subQ14=sQuery(id+"F12.wireOp",EDGE,"E72.1");var subQ16=sQuery(id+"F12.wireOp",EDGE,"E74.1");var subQ18=sQuery(id+"F12.wireOp",EDGE,"E74.8");Q0=qUnion([makeQuery(id+"F12.imprint","IMPRINT",FACE,{"disambiguationData":[TD([[makeQuery(id+"F12.imprint","IMPRINT",EDGE,{"derivedFrom":subQ7}),1.0]])]}),makeQuery(id+"F12.imprint","IMPRINT",FACE,{"disambiguationData":[TD([[makeQuery(id+"F12.imprint","IMPRINT",EDGE,{"derivedFrom":subQ14}),1.0]])]}),makeQuery(id+"F12.imprint","IMPRINT",FACE,{"disambiguationData":[TD([[makeQuery(id+"F12.imprint","IMPRINT",EDGE,{"derivedFrom":subQ16}),1.0]])]}),makeQuery(id+"F12.imprint","IMPRINT",FACE,{"disambiguationData":[TD([[makeQuery(id+"F12.imprint","IMPRINT",EDGE,{"derivedFrom":subQ18}),-1.0]])]})]);}
            var Q1;
            Q1=makeQuery(id+"F5.boolean.opBoolean","SPLIT",FACE,{"disambiguationData":[TD([makeQuery(id+"F5.opExtrude","SWEPT_FACE",FACE,{"disambiguationData":[OSD([sQuery(id+"F4.wireOp",EDGE,"E41")])]})])],"derivedFrom":makeQuery(id+"F3.boolean.opBoolean","COPY",FACE,{"derivedFrom":makeQuery(id+"F3.opExtrude","CAP_FACE",FACE,{"disambiguationData":[OSD([sQuery(id+"F0.wireOp",EDGE,"E25.0"),sQuery(id+"F0.wireOp",EDGE,"E25.1"),sQuery(id+"F0.wireOp",EDGE,"E25.2"),sQuery(id+"F0.wireOp",EDGE,"E25.3"),sQuery(id+"F0.wireOp",EDGE,"E25.4"),sQuery(id+"F0.wireOp",EDGE,"E25.5"),sQuery(id+"F0.wireOp",EDGE,"E25.6"),sQuery(id+"F0.wireOp",EDGE,"E25.7")])],"isStart":false})})});
            extrude(context, id + "F13", {"entities" : qUnion([Q0]), "operationType" : NewBodyOperationType.REMOVE, "endBound" : BoundingType.UP_TO_SURFACE, "endBoundEntityFace" : qUnion([Q1]), "depth" : 25 * mm});
        }
        {
            var Q0;
            Q0=makeQuery(id+"F3.boolean.opBoolean","COPY",EDGE,{"derivedFrom":makeQuery(id+"F3.opExtrude","CAP_EDGE",EDGE,{"disambiguationData":[OSD([sQuery(id+"F0.wireOp",EDGE,"E25.6")])],"isStart":false})});
            var Q1;
            Q1=makeQuery(id+"F8.boolean.opBoolean","INTERSECT",EDGE,{"derivedFrom":[makeQuery(id+"F5.opExtrude","SWEPT_FACE",FACE,{"disambiguationData":[OSD([sQuery(id+"F4.wireOp",EDGE,"E30")])]}),makeQuery(id+"F8.opExtrude","CAP_FACE",FACE,{"disambiguationData":[OSD([sQuery(id+"F7.wireOp",EDGE,"E67")])],"isStart":false})]});
            var Q2;
            Q2=makeQuery(id+"F8.boolean.opBoolean","INTERSECT",EDGE,{"disambiguationData":[OD(1.0)],"derivedFrom":[makeQuery(id+"F5.opExtrude","SWEPT_FACE",FACE,{"disambiguationData":[OSD([sQuery(id+"F4.wireOp",EDGE,"E30")])]}),makeQuery(id+"F8.opExtrude","SWEPT_FACE",FACE,{"disambiguationData":[OSD([sQuery(id+"F7.wireOp",EDGE,"E67")])]})]});
            var Q3;
            {var subQ0=sQuery(id+"F4.wireOp",EDGE,"E30");Q3=makeQuery(id+"F8.boolean.opBoolean","SPLIT",EDGE,{"disambiguationData":[TD([makeQuery(id+"F5.opExtrude","SWEPT_FACE",FACE,{"disambiguationData":[OSD([sQuery(id+"F4.wireOp",EDGE,"E35.filletArc")])]})])],"derivedFrom":makeQuery(id+"F5.opExtrude","CAP_EDGE",EDGE,{"disambiguationData":[OSD([subQ0])],"isStart":false})});}
            var Q4;
            {var subQ0=sQuery(id+"F0.wireOp",EDGE,"E25.7");var subQ1=sQuery(id+"F0.wireOp",EDGE,"E25.1");var subQ2=sQuery(id+"F0.wireOp",EDGE,"E25.6");var subQ3=sQuery(id+"F0.wireOp",EDGE,"E25.5");var subQ4=sQuery(id+"F0.wireOp",EDGE,"E25.4");var subQ5=sQuery(id+"F0.wireOp",EDGE,"E25.0");var subQ6=sQuery(id+"F0.wireOp",EDGE,"E25.2");var subQ7=sQuery(id+"F0.wireOp",EDGE,"E25.3");Q4=makeQuery(id+"F8.boolean.opBoolean","INTERSECT",EDGE,{"derivedFrom":[makeQuery(id+"F5.boolean.opBoolean","SPLIT",FACE,{"disambiguationData":[TD([makeQuery(id+"F2.opExtrude","SWEPT_FACE",FACE,{"disambiguationData":[OSD([subQ5])]})])],"derivedFrom":makeQuery(id+"F3.boolean.opBoolean","COPY",FACE,{"derivedFrom":makeQuery(id+"F3.opExtrude","CAP_FACE",FACE,{"disambiguationData":[OSD([subQ5,subQ1,subQ6,subQ7,subQ4,subQ3,subQ2,subQ0])],"isStart":false})})}),makeQuery(id+"F8.opExtrude","SWEPT_FACE",FACE,{"disambiguationData":[OSD([sQuery(id+"F7.wireOp",EDGE,"E67")])]})]});}
            var Q5;
            Q5=makeQuery(id+"F8.boolean.opBoolean","INTERSECT",EDGE,{"disambiguationData":[OD(0.0)],"derivedFrom":[makeQuery(id+"F5.opExtrude","SWEPT_FACE",FACE,{"disambiguationData":[OSD([sQuery(id+"F4.wireOp",EDGE,"E30")])]}),makeQuery(id+"F8.opExtrude","SWEPT_FACE",FACE,{"disambiguationData":[OSD([sQuery(id+"F7.wireOp",EDGE,"E67")])]})]});
            fillet(context, id + "F14", {"entities" : qUnion([Q0, Q1, Q2, Q3, Q4, Q5]), "radius" : 3 * mm, "tangentPropagation" : true, "allowEdgeOverflow" : false});
        }
        {
            var Q0;
            Q0=makeQuery(id+"F1.opExtrude","CAP_EDGE",EDGE,{"disambiguationData":[OSD([sQuery(id+"F0.wireOp",EDGE,"E1.bottom")])],"isStart":false});
            fillet(context, id + "F15", {"entities" : qUnion([Q0]), "radius" : 2 * mm, "tangentPropagation" : true, "allowEdgeOverflow" : false});
        }
        {
            var Q0;
            {var subQ0=sQuery(id+"F0.wireOp",EDGE,"E22.filletArc");var subQ1=sQuery(id+"F0.wireOp",EDGE,"E7");var subQ2=sQuery(id+"F0.wireOp",EDGE,"E6");var subQ3=sQuery(id+"F0.wireOp",EDGE,"E5");var subQ4=sQuery(id+"F0.wireOp",EDGE,"E4");var subQ5=sQuery(id+"F0.wireOp",EDGE,"E1.bottom");var subQ6=sQuery(id+"F0.wireOp",EDGE,"E21.filletArc");var subQ7=sQuery(id+"F0.wireOp",EDGE,"E1.top");var subQ8=sQuery(id+"F0.wireOp",EDGE,"E1.left");var subQ9=sQuery(id+"F0.wireOp",EDGE,"E1.right");var subQ10=sQuery(id+"F0.wireOp",EDGE,"E23.filletArc");var subQ11=sQuery(id+"F0.wireOp",EDGE,"E24.filletArc");Q0=makeQuery(id+"F2.boolean.opBoolean","SPLIT",FACE,{"disambiguationData":[TD([makeQuery(id+"F1.opExtrude","SWEPT_FACE",FACE,{"disambiguationData":[OSD([subQ5])]})])],"derivedFrom":makeQuery(id+"F1.opExtrude","CAP_FACE",FACE,{"disambiguationData":[OSD([subQ5,subQ7,subQ8,subQ9,subQ4,subQ3,subQ2,subQ1,subQ6,subQ0,subQ10,subQ11])],"isStart":true})});}
            var sketch = newSketch(context, id + "F16", { "sketchPlane" : qUnion([Q0])});
            skLineSegment(sketch, "E79.0", {"start": v(-64.25, 74.25) * mm, "end": v(64.25, 74.25) * mm});
            skLineSegment(sketch, "E80", {"start": v(0, 74.25) * mm, "end": v(0, 104.25) * mm, "construction": true});
            skCircle(sketch, "E81", {"center": v(0, 104.25) * mm, "radius": 6 * mm});
            skArc(sketch, "E82", {"start": v(15, 104.25) * mm, "mid": v(0, 119.25) * mm, "end": v(-15, 104.25) * mm});
            skLineSegment(sketch, "E83", {"start": v(15, 104.25) * mm, "end": v(15, 92.25) * mm});
            skLineSegment(sketch, "E84", {"start": v(-15, 104.25) * mm, "end": v(-15, 92.25) * mm});
            skLineSegment(sketch, "E85", {"start": v(15, 92.25) * mm, "end": v(33, 74.25) * mm});
            skLineSegment(sketch, "E86", {"start": v(-15, 92.25) * mm, "end": v(-33, 74.25) * mm});
            skLineSegment(sketch, "E87", {"start": v(0, 0) * mm, "end": v(-172.84, 0) * mm, "construction": true});
            skLineSegment(sketch, "E88.MirrorCS", {"start": v(15, -92.25) * mm, "end": v(33, -74.25) * mm});
            skLineSegment(sketch, "E89.MirrorCS", {"start": v(15, -104.25) * mm, "end": v(15, -92.25) * mm});
            skArc(sketch, "E90.MirrorCS", {"start": v(15, -104.25) * mm, "mid": v(0, -119.25) * mm, "end": v(-15, -104.25) * mm});
            skLineSegment(sketch, "E91.MirrorCS", {"start": v(-15, -104.25) * mm, "end": v(-15, -92.25) * mm});
            skLineSegment(sketch, "E92.MirrorCS", {"start": v(-15, -92.25) * mm, "end": v(-33, -74.25) * mm});
            skCircle(sketch, "E93.MirrorC", {"center": v(0, -104.25) * mm, "radius": 6 * mm});
            skSolve(sketch);
        }
        {
            var Q0;
            {var subQ0=sQuery(id+"F16.wireOp",EDGE,"E88.MirrorCS");Q0=makeQuery(id+"F16.imprint","IMPRINT",FACE,{"disambiguationData":[TD([[makeQuery(id+"F16.imprint","IMPRINT",EDGE,{"derivedFrom":subQ0}),1.0]])]});}
            var Q1;
            Q1=makeQuery(id+"F16.imprint","IMPRINT",FACE,{"disambiguationData":[TD([[makeQuery(id+"F16.imprint","IMPRINT",EDGE,{"derivedFrom":sQuery(id+"F16.wireOp",EDGE,"E81")}),-1.0]])]});
            extrude(context, id + "F17", {"entities" : qUnion([Q0, Q1]), "depth" : 25 * mm});
        }
        {
            var Q0;
            Q0=makeQuery(id+"F17.opExtrude","CAP_FACE",FACE,{"disambiguationData":[OSD([sQuery(id+"F16.wireOp",EDGE,"E79.0"),sQuery(id+"F16.wireOp",EDGE,"E81"),sQuery(id+"F16.wireOp",EDGE,"E82"),sQuery(id+"F16.wireOp",EDGE,"E83"),sQuery(id+"F16.wireOp",EDGE,"E84"),sQuery(id+"F16.wireOp",EDGE,"E85"),sQuery(id+"F16.wireOp",EDGE,"E86")])],"isStart":false});
            extrude(context, id + "F18", {"entities" : qUnion([Q0]), "operationType" : NewBodyOperationType.ADD, "depth" : 25 * mm});
        }
    });
